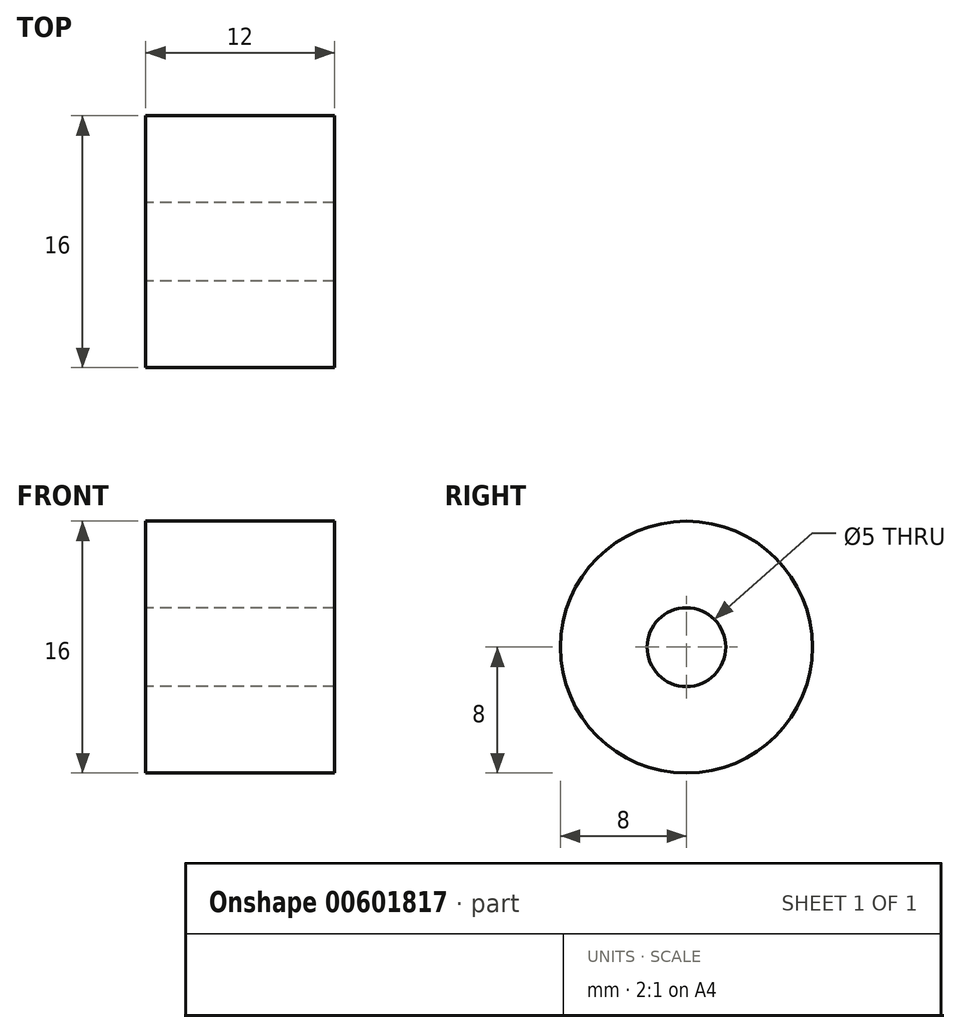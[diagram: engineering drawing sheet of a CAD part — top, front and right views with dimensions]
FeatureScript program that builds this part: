
annotation { "Feature Type Name" : "Feature", "Feature Type Description" : "" }
export const myFeature = defineFeature(function(context is Context, id is Id, definition is map)
    precondition{}
    {
        {
            var Q0;
            Q0=qCreatedBy(makeId("Right.planeOp"),FACE);
            var sketch = newSketch(context, id + "F0", { "sketchPlane" : qUnion([Q0])});
            skCircle(sketch, "E0", {"center": v(0, 0) * mm, "radius": 8 * mm});
            skCircle(sketch, "E1", {"center": v(0, 0) * mm, "radius": 2.5 * mm});
            skSolve(sketch);
        }
        {
            var Q0;
            Q0 = qSketchRegion(id + "F0", true);
            extrude(context, id + "F1", {"entities" : qUnion([Q0]), "depth" : 12 * mm, "offsetDistance" : 25 * mm});
        }
    });
